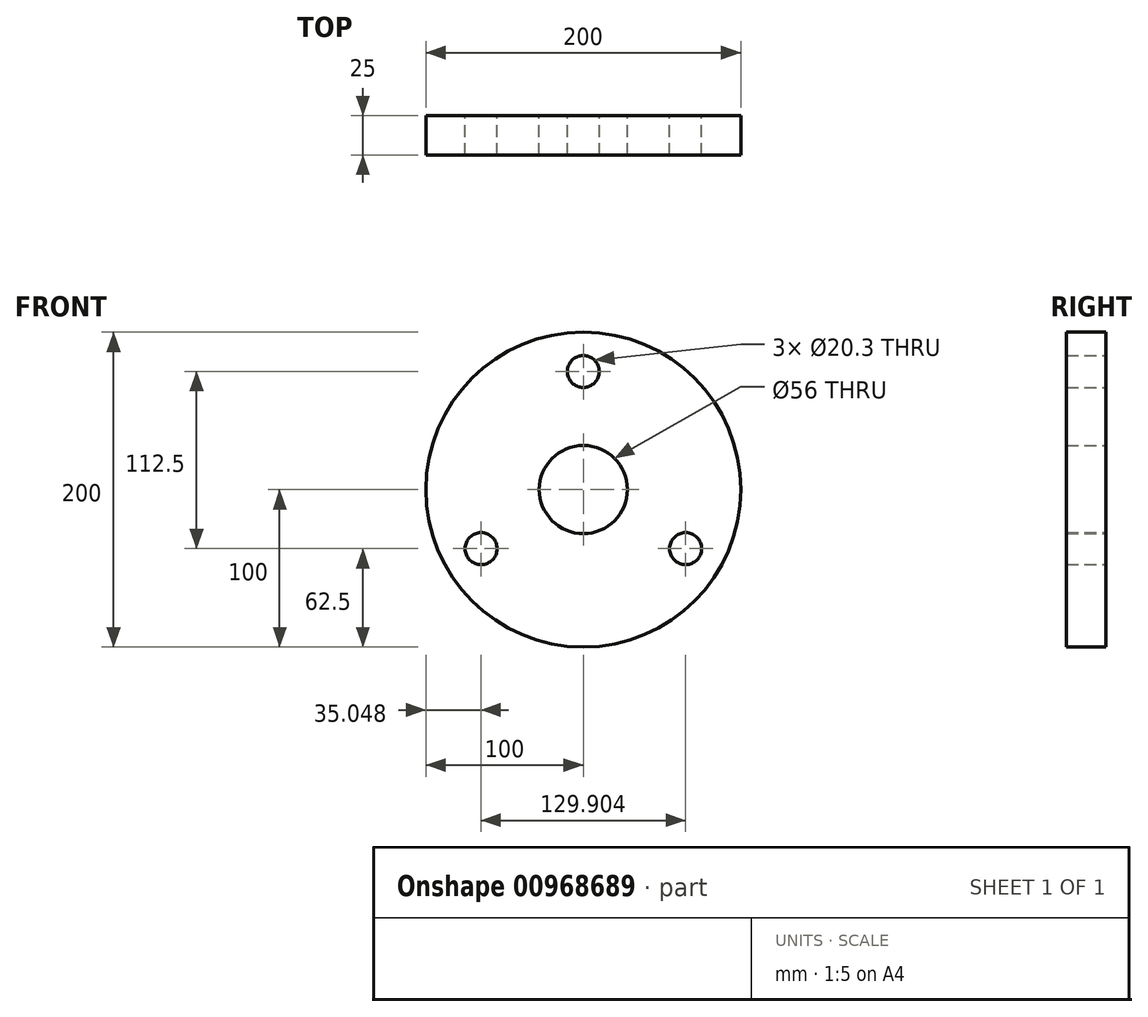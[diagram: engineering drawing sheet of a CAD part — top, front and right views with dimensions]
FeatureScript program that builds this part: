
annotation { "Feature Type Name" : "Feature", "Feature Type Description" : "" }
export const myFeature = defineFeature(function(context is Context, id is Id, definition is map)
    precondition{}
    {
        {
            var Q0;
            Q0=qCreatedBy(makeId("Front.planeOp"),FACE);
            var sketch = newSketch(context, id + "F0", { "sketchPlane" : qUnion([Q0])});
            skCircle(sketch, "E0", {"center": v(0, 0) * mm, "radius": 100 * mm});
            skCircle(sketch, "E1", {"center": v(0, 0) * mm, "radius": 75 * mm, "construction": true});
            skCircle(sketch, "E2", {"center": v(0, 0) * mm, "radius": 28 * mm});
            skLineSegment(sketch, "E3", {"start": v(0, 0) * mm, "end": v(0, 113.3) * mm});
            skCircle(sketch, "E4", {"center": v(0, 75) * mm, "radius": 10.15 * mm});
            skCircle(sketch, "E5.1.0", {"center": v(-64.95, -37.5) * mm, "radius": 10.15 * mm});
            skCircle(sketch, "E5.2.0", {"center": v(64.95, -37.5) * mm, "radius": 10.15 * mm});
            skSolve(sketch);
        }
        {
            var Q0;
            Q0=makeQuery(id+"F0.imprint","IMPRINT",FACE,{"disambiguationData":[TD([[makeQuery(id+"F0.imprint","IMPRINT",EDGE,{"derivedFrom":sQuery(id+"F0.wireOp",EDGE,"E0")}),1.0]])]});
            extrude(context, id + "F1", {"entities" : qUnion([Q0]), "depth" : 25 * mm, "offsetDistance" : 25 * mm});
        }
    });
